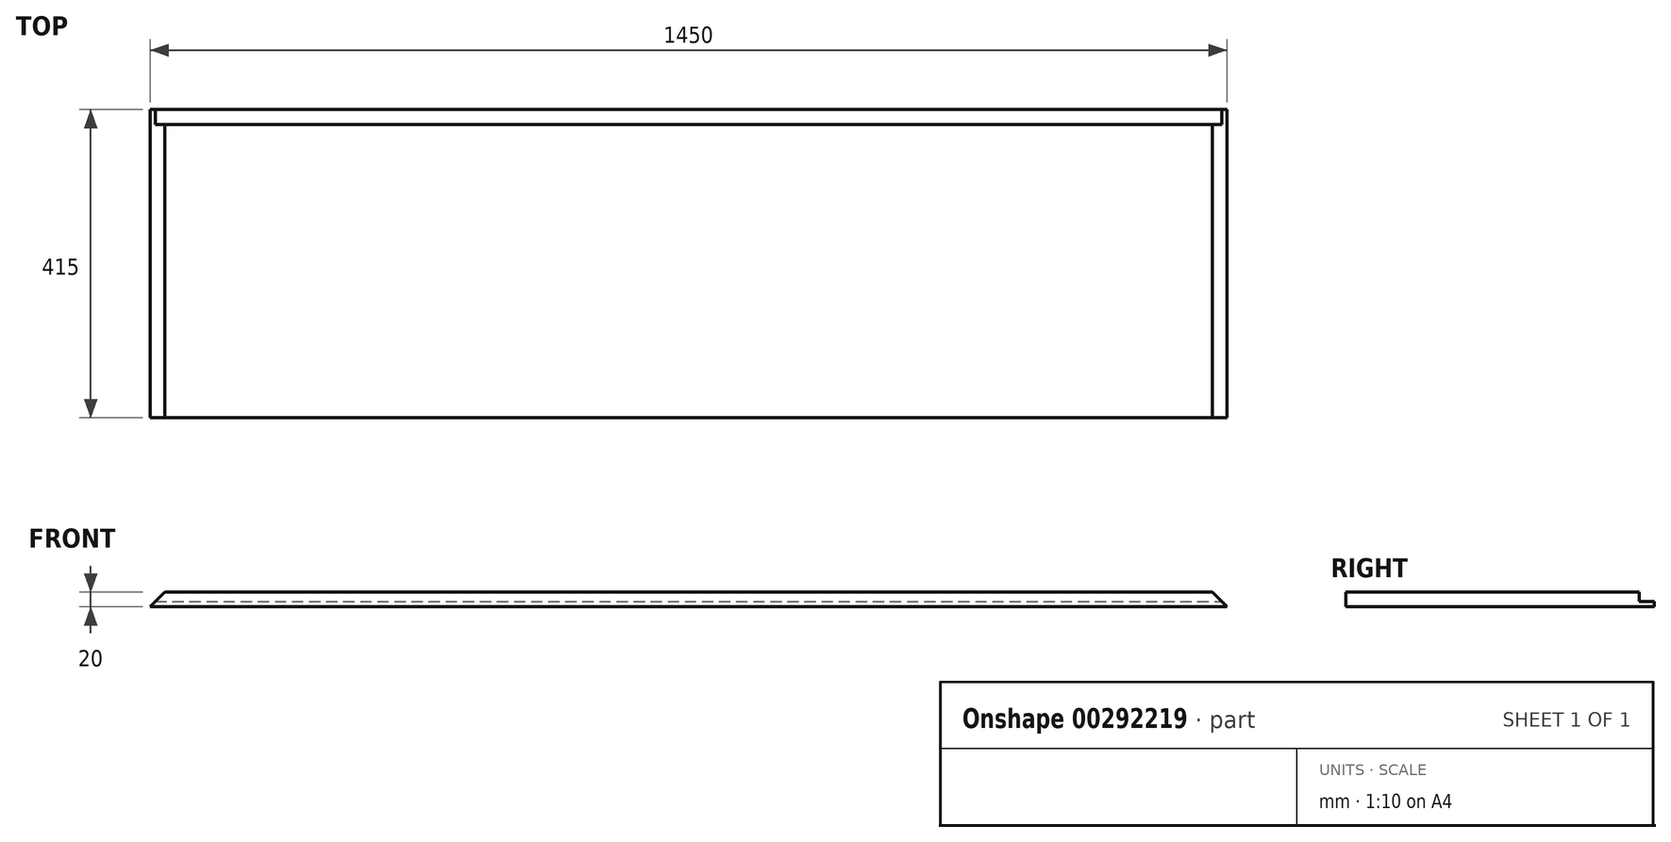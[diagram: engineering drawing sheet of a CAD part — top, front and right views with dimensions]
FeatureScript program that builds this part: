
annotation { "Feature Type Name" : "Feature", "Feature Type Description" : "" }
export const myFeature = defineFeature(function(context is Context, id is Id, definition is map)
    precondition{}
    {
        {
            var Q0;
            Q0=qCreatedBy(makeId("Top.planeOp"),FACE);
            var sketch = newSketch(context, id + "F0", { "sketchPlane" : qUnion([Q0])});
            skPoint(sketch, "E0.middle", {"position": v(0, 0) * mm});
            skLineSegment(sketch, "E1.bottom", {"start": v(725, 207.5) * mm, "end": v(-725, 207.5) * mm});
            skLineSegment(sketch, "E1.top", {"start": v(725, -207.5) * mm, "end": v(-725, -207.5) * mm});
            skLineSegment(sketch, "E1.left", {"start": v(725, 207.5) * mm, "end": v(725, -207.5) * mm});
            skLineSegment(sketch, "E1.right", {"start": v(-725, 207.5) * mm, "end": v(-725, -207.5) * mm});
            skSolve(sketch);
        }
        {
            var Q0;
            Q0 = qSketchRegion(id + "F0", true);
            extrude(context, id + "F1", {"entities" : qUnion([Q0]), "depth" : 20 * mm});
        }
        {
            var Q0;
            Q0=makeQuery(id+"F1.opExtrude","SWEPT_FACE",FACE,{"disambiguationData":[OSD([sQuery(id+"F0.wireOp",EDGE,"E1.left")])]});
            var sketch = newSketch(context, id + "F2", { "sketchPlane" : qUnion([Q0])});
            skLineSegment(sketch, "E2.bottom", {"start": v(207.5, 20) * mm, "end": v(187.5, 20) * mm});
            skLineSegment(sketch, "E2.top", {"start": v(207.5, 7) * mm, "end": v(187.5, 7) * mm});
            skLineSegment(sketch, "E2.left", {"start": v(207.5, 20) * mm, "end": v(207.5, 7) * mm});
            skLineSegment(sketch, "E2.right", {"start": v(187.5, 20) * mm, "end": v(187.5, 7) * mm});
            skSolve(sketch);
        }
        {
            var Q0;
            Q0 = qSketchRegion(id + "F2", true);
            extrude(context, id + "F3", {"entities" : qUnion([Q0]), "operationType" : NewBodyOperationType.REMOVE, "oppositeDirection" : true, "depth" : 1450 * mm});
        }
        {
            var Q0;
            Q0=makeQuery(id+"F1.opExtrude","SWEPT_FACE",FACE,{"disambiguationData":[OSD([sQuery(id+"F0.wireOp",EDGE,"E1.top")])]});
            var sketch = newSketch(context, id + "F4", { "sketchPlane" : qUnion([Q0])});
            skLineSegment(sketch, "E3", {"start": v(725, 20) * mm, "end": v(725, 0) * mm});
            skLineSegment(sketch, "E4", {"start": v(725, 0) * mm, "end": v(705, 20) * mm});
            skLineSegment(sketch, "E5", {"start": v(705, 20) * mm, "end": v(725, 20) * mm});
            skLineSegment(sketch, "E6", {"start": v(-725, 0) * mm, "end": v(-705, 20) * mm});
            skLineSegment(sketch, "E7", {"start": v(-705, 20) * mm, "end": v(-725, 20) * mm});
            skLineSegment(sketch, "E8", {"start": v(-725, 20) * mm, "end": v(-725, 0) * mm});
            skSolve(sketch);
        }
        {
            var Q0;
            Q0 = qSketchRegion(id + "F4", true);
            extrude(context, id + "F5", {"entities" : qUnion([Q0]), "operationType" : NewBodyOperationType.REMOVE, "oppositeDirection" : true, "depth" : 510 * mm});
        }
    });
